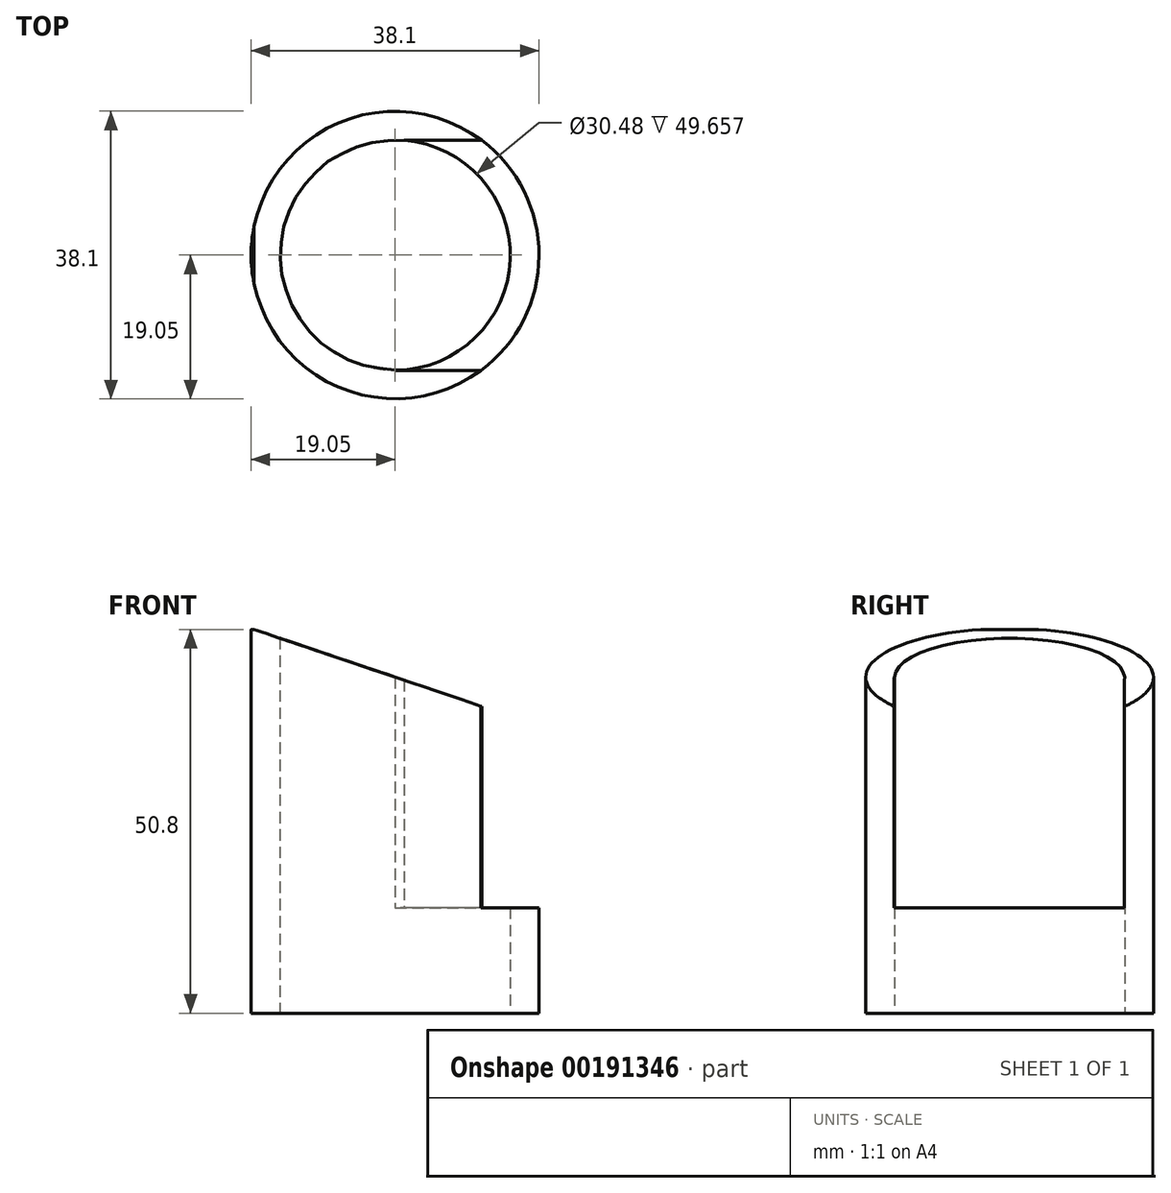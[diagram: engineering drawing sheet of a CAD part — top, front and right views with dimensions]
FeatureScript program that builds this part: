
annotation { "Feature Type Name" : "Feature", "Feature Type Description" : "" }
export const myFeature = defineFeature(function(context is Context, id is Id, definition is map)
    precondition{}
    {
        {
            var Q0;
            Q0=qCreatedBy(makeId("Top.planeOp"),FACE);
            var sketch = newSketch(context, id + "F0", { "sketchPlane" : qUnion([Q0])});
            skCircle(sketch, "E0", {"center": v(0, 0) * mm, "radius": 15.24 * mm});
            skCircle(sketch, "E1", {"center": v(0, 0) * mm, "radius": 19.05 * mm});
            skSolve(sketch);
        }
        {
            var Q0;
            Q0 = qSketchRegion(id + "F0", true);
            extrude(context, id + "F1", {"entities" : qUnion([Q0]), "depth" : 50.8 * mm});
        }
        {
            var Q0;
            Q0=qCreatedBy(makeId("Front.planeOp"),FACE);
            var sketch = newSketch(context, id + "F2", { "sketchPlane" : qUnion([Q0])});
            skLineSegment(sketch, "E2", {"start": v(-19.07, 50.94) * mm, "end": v(19.17, 38) * mm});
            skLineSegment(sketch, "E3", {"start": v(19.17, 50.85) * mm, "end": v(-19.07, 50.94) * mm});
            skLineSegment(sketch, "E4", {"start": v(19.17, 50.85) * mm, "end": v(19.17, 38) * mm});
            skSolve(sketch);
        }
        {
            var Q0;
            Q0 = qSketchRegion(id + "F2", true);
            extrude(context, id + "F3", {"entities" : qUnion([Q0]), "operationType" : NewBodyOperationType.REMOVE, "endBound" : BoundingType.SYMMETRIC, "oppositeDirection" : true, "depth" : 50.8 * mm});
        }
        {
            var Q0;
            Q0=qCreatedBy(makeId("Right.planeOp"),FACE);
            var sketch = newSketch(context, id + "F4", { "sketchPlane" : qUnion([Q0])});
            skLineSegment(sketch, "E5.bottom", {"start": v(-15.29, 44.45) * mm, "end": v(15.2, 44.45) * mm});
            skLineSegment(sketch, "E5.top", {"start": v(-15.29, 13.97) * mm, "end": v(15.2, 13.97) * mm});
            skLineSegment(sketch, "E5.left", {"start": v(-15.29, 44.45) * mm, "end": v(-15.29, 13.97) * mm});
            skLineSegment(sketch, "E5.right", {"start": v(15.2, 44.45) * mm, "end": v(15.2, 13.97) * mm});
            skSolve(sketch);
        }
        {
            var Q0;
            Q0 = qSketchRegion(id + "F4", true);
            extrude(context, id + "F5", {"entities" : qUnion([Q0]), "operationType" : NewBodyOperationType.REMOVE, "depth" : 25.4 * mm});
        }
    });
